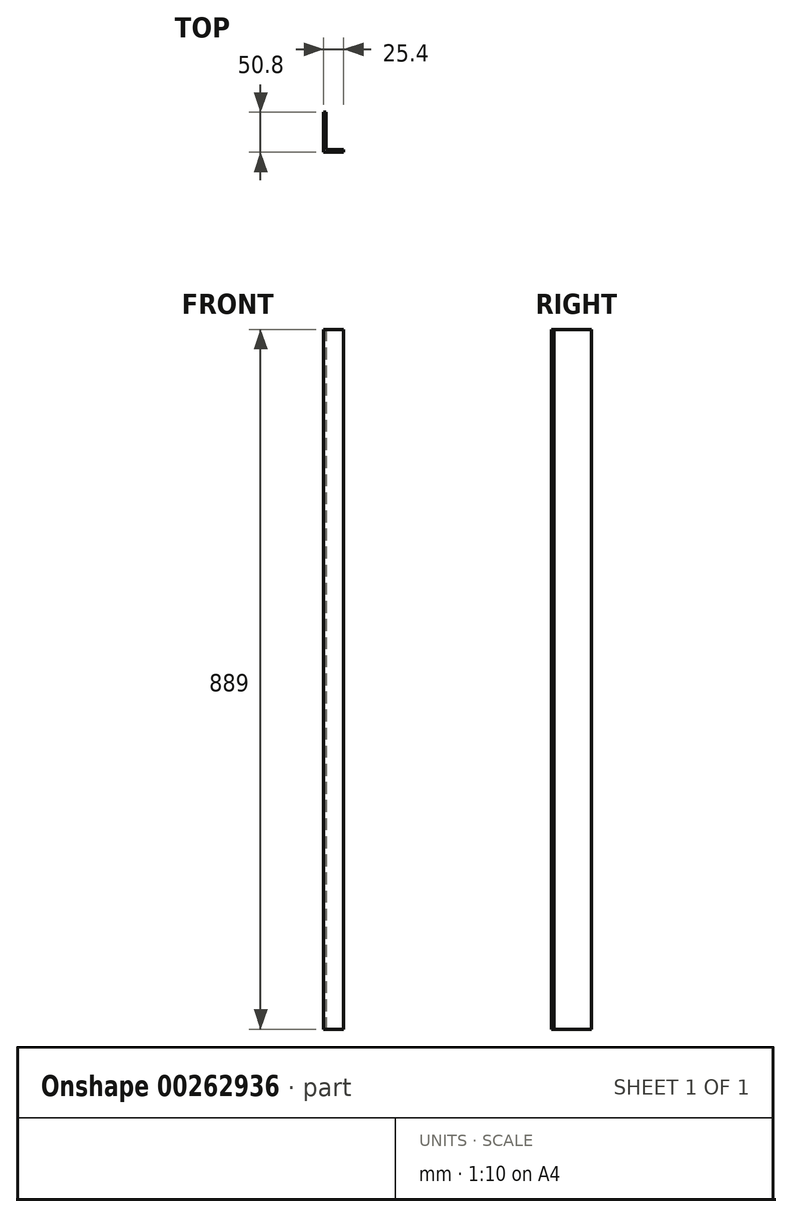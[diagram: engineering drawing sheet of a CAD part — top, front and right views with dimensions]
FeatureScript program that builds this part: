
annotation { "Feature Type Name" : "Feature", "Feature Type Description" : "" }
export const myFeature = defineFeature(function(context is Context, id is Id, definition is map)
    precondition{}
    {
        {
            var Q0;
            Q0=qCreatedBy(makeId("Top.planeOp"),FACE);
            var sketch = newSketch(context, id + "F0", { "sketchPlane" : qUnion([Q0])});
            skLineSegment(sketch, "E0", {"start": v(0, 50.8) * mm, "end": v(0, 0) * mm});
            skLineSegment(sketch, "E1", {"start": v(25.4, 0) * mm, "end": v(25.4, 3.18) * mm});
            skLineSegment(sketch, "E2", {"start": v(25.4, 3.18) * mm, "end": v(3.18, 3.17) * mm});
            skLineSegment(sketch, "E3", {"start": v(3.18, 3.17) * mm, "end": v(3.18, 50.8) * mm});
            skLineSegment(sketch, "E4", {"start": v(3.18, 50.8) * mm, "end": v(0, 50.8) * mm});
            skLineSegment(sketch, "E5", {"start": v(0, 0) * mm, "end": v(25.4, 0) * mm});
            skSolve(sketch);
        }
        {
            var Q0;
            Q0=makeQuery(id+"F0.imprint","IMPRINT",FACE,{"disambiguationData":[TD([[makeQuery(id+"F0.imprint","IMPRINT",EDGE,{"derivedFrom":sQuery(id+"F0.wireOp",EDGE,"E0")}),1.0]])]});
            extrude(context, id + "F1", {"entities" : qUnion([Q0]), "depth" : 889 * mm});
        }
    });
